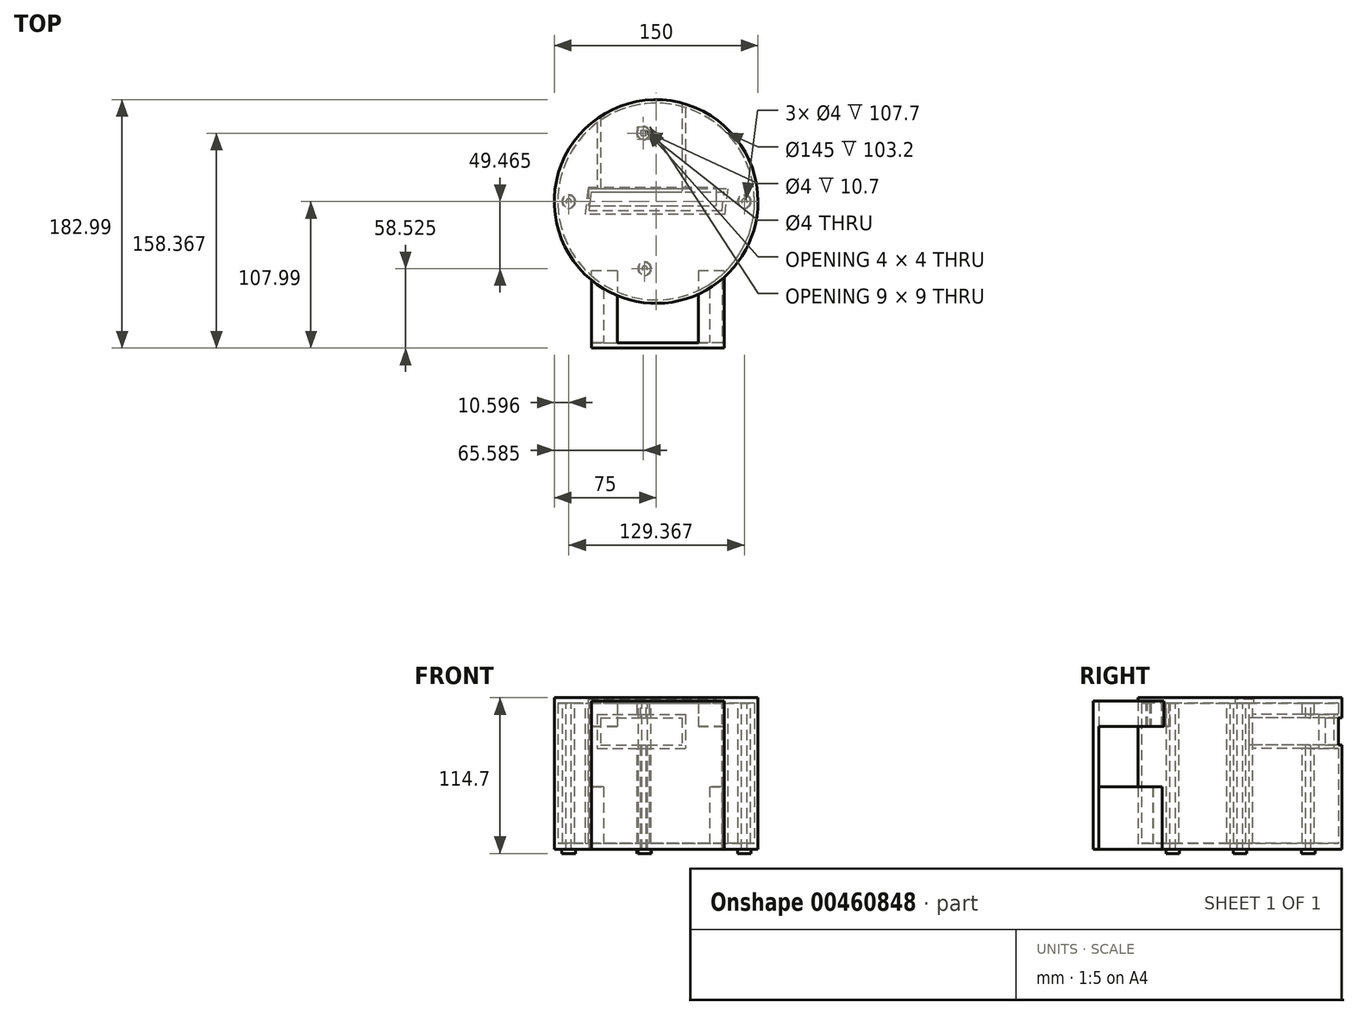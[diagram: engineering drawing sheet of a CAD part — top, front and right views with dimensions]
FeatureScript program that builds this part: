
annotation { "Feature Type Name" : "Feature", "Feature Type Description" : "" }
export const myFeature = defineFeature(function(context is Context, id is Id, definition is map)
    precondition{}
    {
        {
            var Q0;
            Q0=qCreatedBy(makeId("Top.planeOp"),FACE);
            var sketch = newSketch(context, id + "F0", { "sketchPlane" : qUnion([Q0])});
            skCircle(sketch, "E0", {"center": v(0, 0) * mm, "radius": 75 * mm});
            skSolve(sketch);
        }
        {
            var Q0;
            Q0=makeQuery(id+"F0.imprint","IMPRINT",FACE,{"disambiguationData":[TD([[makeQuery(id+"F0.imprint","IMPRINT",EDGE,{"derivedFrom":sQuery(id+"F0.wireOp",EDGE,"E0")}),1.0]])]});
            extrude(context, id + "F1", {"entities" : qUnion([Q0]), "depth" : 105.7 * mm});
        }
        {
            var Q0;
            Q0=makeQuery(id+"F1.opExtrude","CAP_FACE",FACE,{"disambiguationData":[OSD([sQuery(id+"F0.wireOp",EDGE,"E0")])],"isStart":false});
            var sketch = newSketch(context, id + "F2", { "sketchPlane" : qUnion([Q0])});
            skLineSegment(sketch, "E1", {"start": v(0, 0) * mm, "end": v(75, 0) * mm});
            skLineSegment(sketch, "E2", {"start": v(0, 0) * mm, "end": v(-75, 0) * mm});
            skLineSegment(sketch, "E3", {"start": v(-75, 0) * mm, "end": v(-74.67, 7) * mm});
            skLineSegment(sketch, "E4", {"start": v(-74.67, 7) * mm, "end": v(74.67, 7) * mm});
            skLineSegment(sketch, "E5", {"start": v(74.67, 7) * mm, "end": v(74.67, -7) * mm});
            skLineSegment(sketch, "E6", {"start": v(74.67, -7) * mm, "end": v(-74.67, -7) * mm});
            skLineSegment(sketch, "E7", {"start": v(-74.67, -7) * mm, "end": v(-75, 0) * mm});
            skLineSegment(sketch, "E8", {"start": v(42.35, -61.9) * mm, "end": v(55.05, 50.93) * mm});
            skLineSegment(sketch, "E9", {"start": v(-53.95, -52.1) * mm, "end": v(-41.9, 62.2) * mm});
            skSolve(sketch);
        }
        {
            var Q0;
            {var subQ1=sQuery(id+"F2.wireOp",EDGE,"E1");var subQ7=sQuery(id+"F2.wireOp",EDGE,"E2");var subQ8=makeQuery(id+"F2.imprint","INTERSECT",VERTEX,{"derivedFrom":[subQ1,subQ7]});Q0=makeQuery(id+"F2.imprint","IMPRINT",FACE,{"disambiguationData":[TD([[makeQuery(id+"F2.imprint","IMPRINT",EDGE,{"disambiguationData":[TD([[subQ8,-1.0]])],"derivedFrom":subQ1}),-1.0]])]});}
            var Q1;
            {var subQ1=sQuery(id+"F2.wireOp",EDGE,"E1");var subQ7=sQuery(id+"F2.wireOp",EDGE,"E2");var subQ8=makeQuery(id+"F2.imprint","INTERSECT",VERTEX,{"derivedFrom":[subQ1,subQ7]});Q1=makeQuery(id+"F2.imprint","IMPRINT",FACE,{"disambiguationData":[TD([[makeQuery(id+"F2.imprint","IMPRINT",EDGE,{"disambiguationData":[TD([[subQ8,-1.0]])],"derivedFrom":subQ1}),1.0]])]});}
            extrude(context, id + "F3", {"entities" : qUnion([Q0, Q1]), "operationType" : NewBodyOperationType.REMOVE, "oppositeDirection" : true, "depth" : 148 * mm});
        }
        {
            var Q0;
            Q0=makeQuery(id+"F1.opExtrude","CAP_FACE",FACE,{"disambiguationData":[OSD([sQuery(id+"F0.wireOp",EDGE,"E0")])],"isStart":false});
            var sketch = newSketch(context, id + "F4", { "sketchPlane" : qUnion([Q0])});
            skCircle(sketch, "E10", {"center": v(-8.44, -49.46) * mm, "radius": 2 * mm});
            skCircle(sketch, "E11", {"center": v(-9.41, 50.38) * mm, "radius": 2 * mm});
            skCircle(sketch, "E12", {"center": v(64.96, 0) * mm, "radius": 2 * mm});
            skCircle(sketch, "E13", {"center": v(-64.4, 0) * mm, "radius": 2 * mm});
            skSolve(sketch);
        }
        {
            var Q0;
            Q0=makeQuery(id+"F4.imprint","IMPRINT",FACE,{"disambiguationData":[TD([[makeQuery(id+"F4.imprint","IMPRINT",EDGE,{"derivedFrom":sQuery(id+"F4.wireOp",EDGE,"E10")}),1.0]])]});
            var Q1;
            Q1=makeQuery(id+"F4.imprint","IMPRINT",FACE,{"disambiguationData":[TD([[makeQuery(id+"F4.imprint","IMPRINT",EDGE,{"derivedFrom":sQuery(id+"F4.wireOp",EDGE,"E13")}),1.0]])]});
            var Q2;
            Q2=makeQuery(id+"F4.imprint","IMPRINT",FACE,{"disambiguationData":[TD([[makeQuery(id+"F4.imprint","IMPRINT",EDGE,{"derivedFrom":sQuery(id+"F4.wireOp",EDGE,"E11")}),1.0]])]});
            var Q3;
            Q3=makeQuery(id+"F4.imprint","IMPRINT",FACE,{"disambiguationData":[TD([[makeQuery(id+"F4.imprint","IMPRINT",EDGE,{"derivedFrom":sQuery(id+"F4.wireOp",EDGE,"E12")}),1.0]])]});
            extrude(context, id + "F5", {"entities" : qUnion([Q0, Q1, Q2, Q3]), "operationType" : NewBodyOperationType.REMOVE, "oppositeDirection" : true, "depth" : 332 * mm});
        }
        {
            var Q0;
            Q0=makeQuery(id+"F3.boolean.opBoolean","COPY",FACE,{"derivedFrom":makeQuery(id+"F3.opExtrude","SWEPT_FACE",FACE,{"disambiguationData":[OSD([sQuery(id+"F2.wireOp",EDGE,"E4")])]})});
            var sketch = newSketch(context, id + "F6", { "sketchPlane" : qUnion([Q0])});
            skLineSegment(sketch, "E14.bottom", {"start": v(-41.03, 75) * mm, "end": v(18.97, 75) * mm});
            skLineSegment(sketch, "E14.top", {"start": v(-41.03, 95) * mm, "end": v(18.97, 95) * mm});
            skLineSegment(sketch, "E14.left", {"start": v(-41.03, 75) * mm, "end": v(-41.03, 95) * mm});
            skLineSegment(sketch, "E14.right", {"start": v(18.97, 75) * mm, "end": v(18.97, 95) * mm});
            skSolve(sketch);
        }
        {
            var Q0;
            Q0=makeQuery(id+"F6.imprint","IMPRINT",FACE,{"disambiguationData":[TD([[makeQuery(id+"F6.imprint","IMPRINT",EDGE,{"derivedFrom":sQuery(id+"F6.wireOp",EDGE,"E14.bottom")}),1.0]])]});
            extrude(context, id + "F7", {"entities" : qUnion([Q0]), "operationType" : NewBodyOperationType.REMOVE, "oppositeDirection" : true, "depth" : 89 * mm});
        }
        {
            var Q0;
            Q0=makeQuery(id+"F1.opExtrude","CAP_FACE",FACE,{"disambiguationData":[OSD([sQuery(id+"F0.wireOp",EDGE,"E0")])],"isStart":false});
            shell(context, id + "F8", {"entities" : qUnion([Q0]), "thickness" : 2.5 * mm});
        }
        {
            var Q0;
            Q0=makeQuery(id+"F1.opExtrude","CAP_FACE",FACE,{"disambiguationData":[OSD([sQuery(id+"F0.wireOp",EDGE,"E0")])],"isStart":false});
            var sketch = newSketch(context, id + "F9", { "sketchPlane" : qUnion([Q0])});
            skCircle(sketch, "E15", {"center": v(0, 0) * mm, "radius": 75 * mm});
            skSolve(sketch);
        }
        {
            var Q0;
            Q0 = qSketchRegion(id + "F9", true);
            extrude(context, id + "F10", {"entities" : qUnion([Q0]), "depth" : 3 * mm});
        }
        {
            var Q0;
            Q0=makeQuery(id+"F10.opExtrude","CAP_FACE",FACE,{"disambiguationData":[OSD([sQuery(id+"F9.wireOp",EDGE,"E15")])],"isStart":false});
            var sketch = newSketch(context, id + "F11", { "sketchPlane" : qUnion([Q0])});
            skLineSegment(sketch, "E16.bottom", {"start": v(-49.98, 10.42) * mm, "end": v(44.23, 10.42) * mm});
            skLineSegment(sketch, "E16.top", {"start": v(-49.98, -3.24) * mm, "end": v(44.23, -3.24) * mm});
            skLineSegment(sketch, "E16.left", {"start": v(-49.98, 10.42) * mm, "end": v(-49.98, -3.24) * mm});
            skLineSegment(sketch, "E16.right", {"start": v(44.23, 10.42) * mm, "end": v(44.23, -3.24) * mm});
            skSolve(sketch);
        }
        {
            var Q0;
            Q0=makeQuery(id+"F11.imprint","IMPRINT",FACE,{"disambiguationData":[TD([[makeQuery(id+"F11.imprint","IMPRINT",EDGE,{"derivedFrom":sQuery(id+"F11.wireOp",EDGE,"E16.bottom")}),-1.0]])]});
            extrude(context, id + "F12", {"entities" : qUnion([Q0]), "operationType" : NewBodyOperationType.REMOVE, "oppositeDirection" : true, "depth" : 3 * mm});
        }
        {
            var Q0;
            Q0=makeQuery(id+"F1.opExtrude","CAP_FACE",FACE,{"disambiguationData":[OSD([sQuery(id+"F0.wireOp",EDGE,"E0")])],"isStart":true});
            var sketch = newSketch(context, id + "F13", { "sketchPlane" : qUnion([Q0])});
            skCircle(sketch, "E17", {"center": v(0, 0) * mm, "radius": 75 * mm});
            skSolve(sketch);
        }
        {
            var Q0;
            Q0=makeQuery(id+"F13.imprint","IMPRINT",FACE,{"disambiguationData":[TD([[makeQuery(id+"F13.imprint","IMPRINT",EDGE,{"derivedFrom":sQuery(id+"F13.wireOp",EDGE,"E17")}),-1.0]])]});
            extrude(context, id + "F14", {"entities" : qUnion([Q0]), "depth" : 2 * mm});
        }
        {
            var Q0;
            {var subQ3=sQuery(id+"F9.wireOp",EDGE,"E15");Q0=makeQuery(id+"F6oyR5sGcbJv1ea_2.boolean.opBoolean","SPLIT",FACE,{"disambiguationData":[TD([makeQuery(id+"F12.boolean.opBoolean","COPY",FACE,{"derivedFrom":makeQuery(id+"F12.opExtrude","SWEPT_FACE",FACE,{"disambiguationData":[OSD([sQuery(id+"F11.wireOp",EDGE,"E16.bottom")])]})})])],"derivedFrom":makeQuery(id+"F10.opExtrude","CAP_FACE",FACE,{"disambiguationData":[OSD([subQ3])],"isStart":false})});}
            var sketch = newSketch(context, id + "F15", { "sketchPlane" : qUnion([Q0])});
            skLineSegment(sketch, "E18.bottom", {"start": v(-49.98, 10.42) * mm, "end": v(44.23, 10.42) * mm});
            skLineSegment(sketch, "E18.top", {"start": v(-49.98, -3.24) * mm, "end": v(44.23, -3.24) * mm});
            skLineSegment(sketch, "E18.left", {"start": v(-49.98, 10.42) * mm, "end": v(-49.98, -3.24) * mm});
            skLineSegment(sketch, "E18.right", {"start": v(44.23, 10.42) * mm, "end": v(44.23, -3.24) * mm});
            skSolve(sketch);
        }
        {
            var Q0;
            Q0=makeQuery(id+"F10.opExtrude","CAP_FACE",FACE,{"disambiguationData":[OSD([sQuery(id+"F9.wireOp",EDGE,"E15")])],"isStart":false});
            var Q1;
            Q1=makeQuery(id+"F15.imprint","IMPRINT",FACE,{"disambiguationData":[TD([[makeQuery(id+"F15.imprint","IMPRINT",EDGE,{"derivedFrom":sQuery(id+"F15.wireOp",EDGE,"E18.bottom")}),-1.0]])]});
            extrude(context, id + "F16", {"entities" : qUnion([Q0, Q1]), "operationType" : NewBodyOperationType.ADD, "depth" : 1 * mm});
        }
        {
            var Q0;
            Q0=makeQuery(id+"F14.opExtrude","CAP_FACE",FACE,{"disambiguationData":[OSD([sQuery(id+"F0.wireOp",EDGE,"E0"),sQuery(id+"F2.wireOp",EDGE,"E4"),sQuery(id+"F2.wireOp",EDGE,"E6"),sQuery(id+"F2.wireOp",EDGE,"E8"),sQuery(id+"F2.wireOp",EDGE,"E9"),sQuery(id+"F4.wireOp",EDGE,"E10"),sQuery(id+"F4.wireOp",EDGE,"E11"),sQuery(id+"F4.wireOp",EDGE,"E12"),sQuery(id+"F4.wireOp",EDGE,"E13"),sQuery(id+"F13.wireOp",EDGE,"E17")])],"isStart":false});
            var sketch = newSketch(context, id + "F17", { "sketchPlane" : qUnion([Q0])});
            skLineSegment(sketch, "E19.bottom", {"start": v(48.53, 7) * mm, "end": v(39.53, 7) * mm});
            skLineSegment(sketch, "E19.top", {"start": v(48.53, 104) * mm, "end": v(39.53, 104) * mm});
            skLineSegment(sketch, "E19.left", {"start": v(48.53, 7) * mm, "end": v(48.53, 104) * mm});
            skLineSegment(sketch, "E19.right", {"start": v(39.53, 7) * mm, "end": v(39.53, 104) * mm});
            skLineSegment(sketch, "E20.bottom", {"start": v(-38.72, 7) * mm, "end": v(-47.72, 7) * mm});
            skLineSegment(sketch, "E20.top", {"start": v(-38.72, 104) * mm, "end": v(-47.72, 104) * mm});
            skLineSegment(sketch, "E20.left", {"start": v(-38.72, 7) * mm, "end": v(-38.72, 104) * mm});
            skLineSegment(sketch, "E20.right", {"start": v(-47.72, 7) * mm, "end": v(-47.72, 104) * mm});
            skSolve(sketch);
        }
        {
            var Q0;
            {var subQ0=sQuery(id+"F17.wireOp",EDGE,"E20.top");Q0=makeQuery(id+"F17.imprint","IMPRINT",FACE,{"disambiguationData":[TD([[makeQuery(id+"F17.imprint","IMPRINT",EDGE,{"derivedFrom":subQ0}),1.0]])]});}
            var Q1;
            {var subQ0=sQuery(id+"F17.wireOp",EDGE,"E19.top");Q1=makeQuery(id+"F17.imprint","IMPRINT",FACE,{"disambiguationData":[TD([[makeQuery(id+"F17.imprint","IMPRINT",EDGE,{"derivedFrom":subQ0}),1.0]])]});}
            extrude(context, id + "F18", {"entities" : qUnion([Q0, Q1]), "operationType" : NewBodyOperationType.ADD, "oppositeDirection" : true, "depth" : 46 * mm});
        }
        {
            var Q0;
            Q0=makeQuery(id+"F18.opExtrude","SWEPT_FACE",FACE,{"disambiguationData":[OSD([sQuery(id+"F17.wireOp",EDGE,"E20.top")])]});
            var sketch = newSketch(context, id + "F19", { "sketchPlane" : qUnion([Q0])});
            skLineSegment(sketch, "E21.bottom", {"start": v(-47.72, -2) * mm, "end": v(50.08, -2) * mm});
            skLineSegment(sketch, "E21.top", {"start": v(-47.72, 107.38) * mm, "end": v(50.08, 107.38) * mm});
            skLineSegment(sketch, "E21.left", {"start": v(-47.72, -2) * mm, "end": v(-47.72, 107.38) * mm});
            skLineSegment(sketch, "E21.right", {"start": v(50.08, -2) * mm, "end": v(50.08, 107.38) * mm});
            skSolve(sketch);
        }
        {
            var Q0;
            {var subQ3=sQuery(id+"F19.wireOp",EDGE,"E21.top");Q0=makeQuery(id+"F19.imprint","IMPRINT",FACE,{"disambiguationData":[TD([[makeQuery(id+"F19.imprint","IMPRINT",EDGE,{"derivedFrom":subQ3}),-1.0]])]});}
            var Q1;
            {var subQ1=sQuery(id+"F17.wireOp",EDGE,"E20.top");var subQ5=makeQuery(id+"F18.opExtrude","CAP_EDGE",EDGE,{"disambiguationData":[OSD([subQ1])],"isStart":false});Q1=makeQuery(id+"F19.imprint","IMPRINT",FACE,{"disambiguationData":[TD([[makeQuery(id+"F19.imprint","IMPRINT",EDGE,{"derivedFrom":subQ5}),1.0]])]});}
            extrude(context, id + "F20", {"entities" : qUnion([Q0, Q1]), "operationType" : NewBodyOperationType.ADD, "depth" : 4 * mm});
        }
        {
            var Q0;
            {var subQ0=sQuery(id+"F13.wireOp",EDGE,"E17");Q0=makeQuery(id+"F20.boolean.opBoolean","MERGE",FACE,{"derivedFrom":[makeQuery(id+"F18.boolean.opBoolean","MERGE",FACE,{"derivedFrom":[makeQuery(id+"F14.opExtrude","CAP_FACE",FACE,{"disambiguationData":[OSD([sQuery(id+"F0.wireOp",EDGE,"E0"),sQuery(id+"F2.wireOp",EDGE,"E4"),sQuery(id+"F2.wireOp",EDGE,"E6"),sQuery(id+"F2.wireOp",EDGE,"E8"),sQuery(id+"F2.wireOp",EDGE,"E9"),sQuery(id+"F4.wireOp",EDGE,"E10"),sQuery(id+"F4.wireOp",EDGE,"E11"),sQuery(id+"F4.wireOp",EDGE,"E12"),sQuery(id+"F4.wireOp",EDGE,"E13"),subQ0])],"isStart":false}),makeQuery(id+"F18.opExtrude","CAP_FACE",FACE,{"disambiguationData":[OSD([subQ0,sQuery(id+"F17.wireOp",EDGE,"E19.top"),sQuery(id+"F17.wireOp",EDGE,"E19.left"),sQuery(id+"F17.wireOp",EDGE,"E19.right")])],"isStart":true}),makeQuery(id+"F18.opExtrude","CAP_FACE",FACE,{"disambiguationData":[OSD([subQ0,sQuery(id+"F17.wireOp",EDGE,"E20.top"),sQuery(id+"F17.wireOp",EDGE,"E20.left"),sQuery(id+"F17.wireOp",EDGE,"E20.right")])],"isStart":true})]}),makeQuery(id+"F20.opExtrude","SWEPT_FACE",FACE,{"disambiguationData":[OSD([sQuery(id+"F19.wireOp",EDGE,"E21.bottom")])]})]});}
            var sketch = newSketch(context, id + "F21", { "sketchPlane" : qUnion([Q0])});
            skCircle(sketch, "E22", {"center": v(-9.41, -50.38) * mm, "radius": 5 * mm});
            skCircle(sketch, "E23", {"center": v(64.96, 0) * mm, "radius": 5 * mm});
            skCircle(sketch, "E24", {"center": v(-64.4, 0) * mm, "radius": 5 * mm});
            skCircle(sketch, "E25", {"center": v(-8.44, 49.46) * mm, "radius": 5 * mm});
            skSolve(sketch);
        }
        {
            var Q0;
            Q0 = qSketchRegion(id + "F21", true);
            extrude(context, id + "F22", {"entities" : qUnion([Q0]), "depth" : 3 * mm});
        }
        {
            var Q0;
            Q0=makeQuery(id+"F20.opExtrude","CAP_FACE",FACE,{"disambiguationData":[OSD([sQuery(id+"F19.wireOp",EDGE,"E21.bottom"),sQuery(id+"F19.wireOp",EDGE,"E21.top"),sQuery(id+"F19.wireOp",EDGE,"E21.left"),sQuery(id+"F19.wireOp",EDGE,"E21.right")])],"isStart":true});
            var sketch = newSketch(context, id + "F23", { "sketchPlane" : qUnion([Q0])});
            skLineSegment(sketch, "E26.bottom", {"start": v(47.72, 107.38) * mm, "end": v(28.72, 107.38) * mm});
            skLineSegment(sketch, "E26.top", {"start": v(47.72, 88.38) * mm, "end": v(28.72, 88.38) * mm});
            skLineSegment(sketch, "E26.left", {"start": v(47.72, 107.38) * mm, "end": v(47.72, 88.38) * mm});
            skLineSegment(sketch, "E26.right", {"start": v(28.72, 107.38) * mm, "end": v(28.72, 88.38) * mm});
            skLineSegment(sketch, "E27.bottom", {"start": v(-50.08, 107.38) * mm, "end": v(-31.08, 107.38) * mm});
            skLineSegment(sketch, "E27.top", {"start": v(-50.08, 88.38) * mm, "end": v(-31.08, 88.38) * mm});
            skLineSegment(sketch, "E27.left", {"start": v(-50.08, 107.38) * mm, "end": v(-50.08, 88.38) * mm});
            skLineSegment(sketch, "E27.right", {"start": v(-31.08, 107.38) * mm, "end": v(-31.08, 88.38) * mm});
            skLineSegment(sketch, "E28.bottom", {"start": v(28.72, 107.38) * mm, "end": v(-31.08, 107.38) * mm});
            skLineSegment(sketch, "E28.top", {"start": v(28.72, 109.37) * mm, "end": v(-31.08, 109.37) * mm});
            skLineSegment(sketch, "E28.left", {"start": v(28.72, 107.38) * mm, "end": v(28.72, 109.37) * mm});
            skLineSegment(sketch, "E28.right", {"start": v(-31.08, 107.38) * mm, "end": v(-31.08, 109.37) * mm});
            skSolve(sketch);
        }
        {
            var Q0;
            Q0=makeQuery(id+"F23.imprint","IMPRINT",FACE,{"disambiguationData":[TD([[makeQuery(id+"F23.imprint","IMPRINT",EDGE,{"derivedFrom":sQuery(id+"F23.wireOp",EDGE,"E26.bottom")}),1.0]])]});
            var Q1;
            Q1=makeQuery(id+"F23.imprint","IMPRINT",FACE,{"disambiguationData":[TD([[makeQuery(id+"F23.imprint","IMPRINT",EDGE,{"derivedFrom":sQuery(id+"F23.wireOp",EDGE,"E27.bottom")}),1.0]])]});
            extrude(context, id + "F24", {"entities" : qUnion([Q0, Q1]), "operationType" : NewBodyOperationType.ADD, "depth" : 52.8 * mm});
        }
    });
